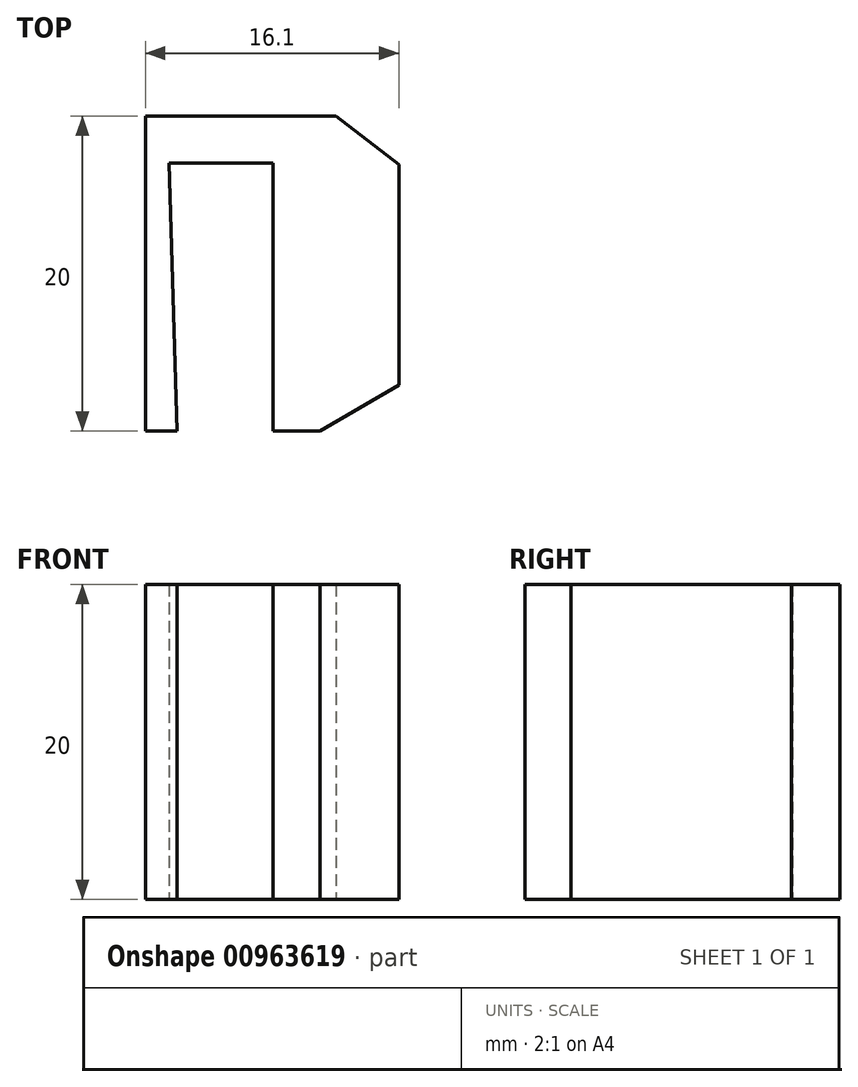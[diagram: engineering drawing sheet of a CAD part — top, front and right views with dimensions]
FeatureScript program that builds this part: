
annotation { "Feature Type Name" : "Feature", "Feature Type Description" : "" }
export const myFeature = defineFeature(function(context is Context, id is Id, definition is map)
    precondition{}
    {
        {
            var Q0;
            Q0=qCreatedBy(makeId("Top.planeOp"),FACE);
            var sketch = newSketch(context, id + "F0", { "sketchPlane" : qUnion([Q0])});
            skLineSegment(sketch, "E0", {"start": v(-33.94, -23.13) * mm, "end": v(-33.94, -3.13) * mm});
            skLineSegment(sketch, "E1", {"start": v(-33.94, -23.13) * mm, "end": v(-31.94, -23.13) * mm});
            skLineSegment(sketch, "E2", {"start": v(-31.94, -23.13) * mm, "end": v(-32.44, -6.13) * mm});
            skLineSegment(sketch, "E3", {"start": v(-33.94, -3.13) * mm, "end": v(-21.84, -3.13) * mm});
            skLineSegment(sketch, "E4", {"start": v(-25.84, -23.13) * mm, "end": v(-22.84, -23.13) * mm});
            skLineSegment(sketch, "E5", {"start": v(-25.84, -23.13) * mm, "end": v(-25.84, -6.13) * mm});
            skLineSegment(sketch, "E6", {"start": v(-25.84, -6.13) * mm, "end": v(-32.44, -6.13) * mm});
            skLineSegment(sketch, "E7", {"start": v(-21.84, -3.13) * mm, "end": v(-17.84, -6.2) * mm});
            skLineSegment(sketch, "E8", {"start": v(-17.84, -6.2) * mm, "end": v(-17.84, -20.2) * mm});
            skLineSegment(sketch, "E9", {"start": v(-17.84, -20.2) * mm, "end": v(-22.84, -23.13) * mm});
            skSolve(sketch);
        }
        {
            var Q0;
            Q0 = qSketchRegion(id + "F0", true);
            extrude(context, id + "F1", {"entities" : qUnion([Q0]), "endBound" : BoundingType.SYMMETRIC, "depth" : 20 * mm, "offsetDistance" : 25 * mm});
        }
    });
